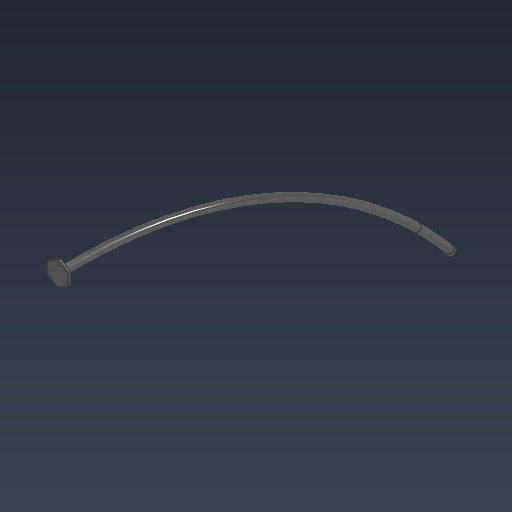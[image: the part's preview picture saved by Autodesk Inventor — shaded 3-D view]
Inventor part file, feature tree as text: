
AUTODESK INVENTOR PART (.ipt)
format: ipt  version: 2021 (Build 250183000, 183)  size: 416,768 bytes
history: native  units: mm
features: sketch x10, extrude x7, fillet x4, sweep x2, plane x2, split x1, hole x1, chamfer x1, projected_geometry x1
ambient origin geometry x8: Origin, YZ Plane, XZ Plane, XY Plane, X Axis, Y Axis, Z Axis, Center Point
bodies: Solid1 (feature_tree), Solid2 (feature_tree), Solid3 (feature_tree)
feature tree (29):
  sketch  "Sketch1"  dims[d0=3300.0mm d1=1650.0mm]
  sweep  "Sweep1"
  sweep  "Sweep2"
  extrude  "Extrusion1"  Depth=23.4mm
  extrude  "Extrusion2"  Depth=1650.0mm
  fillet  "Fillet2"  [1 undecoded]
  plane  "Work Plane1"
  extrude  "Extrusion4"  Depth=3402.0mm
  extrude  "Extrusion5"  Depth=1050.0mm
  extrude  "Extrusion6"  Depth=1701.0mm
  fillet  "Fillet3"  Radius=51.0mm
  extrude  "Extrusion9"  TaperAngle=0.0deg  [1 undecoded]
  extrude  "Extrusion10"  Depth=3.5mm
  fillet  "Fillet6"  Radius=5.0mm
  plane  "Work Plane2"
  split  "Split1"
  fillet  "Fillet7"  [1 undecoded]
  hole  "Hole1"  [1 undecoded]
  chamfer  "Chamfer1"  Angle=120.0deg  [1 undecoded]
  sketch  "Sketch2"  dims[d2=0.0mm d3=25.4mm]
  sketch  "Sketch3"  dims[d4=0.0mm d5=0.0mm d6=23.4mm]
  sketch  "Sketch4"  dims[d7=0.0mm d8=1650.0mm d9=0.0mm d10=0.0mm]
  sketch  "Sketch5"  dims[d11=1752.0mm d12=3402.0mm]
  sketch  "Sketch6"  dims[d13=1701.0mm d14=1050.0mm]
  sketch  "Sketch7"  dims[d15=1701.0mm d16=1701.0mm d17=51.0mm]
  sketch  "Sketch10"  dims[d18=51.0mm d19=0.0mm]
  sketch  "Sketch13"  dims[d20=7.0mm d21=3.5mm d22=5.0mm d23=0.0mm]
  sketch  "Sketch14"  dims[d25=2.0mm d26=-1250.0mm d32=120.0deg d33=120.0deg d34=40.0mm d35=120.0deg d36=120.0deg d37=120.0deg d38=10.0mm d39=0.0mm d40=3300.0mm d41=100.0mm d42=100.0mm d43=0.0mm d44=10.0mm d45=0.0mm d46=1.0mm d53=10.0mm d54=0.0mm d55=7.0mm d56=10.0mm d57=0.0mm d60=3.0mm d61=1.0mm d62=-170.0mm d63=5.0mm d64=12.5mm d65=12.5mm d66=12.5mm d67=8.0mm d68=6.0mm d69=4.0mm d70=2.0mm d71=90.0deg d72=8.0mm d73=20.594885mm d74=1.0mm d75=2.0mm d76=45.0deg]
  projected_geometry  "Projected Loop1"
note: 5 required parameter values undecoded (feature->parameter linkage not recoverable at this tier; creation-order binding heuristic only, values carry confidence <= 0.55)
